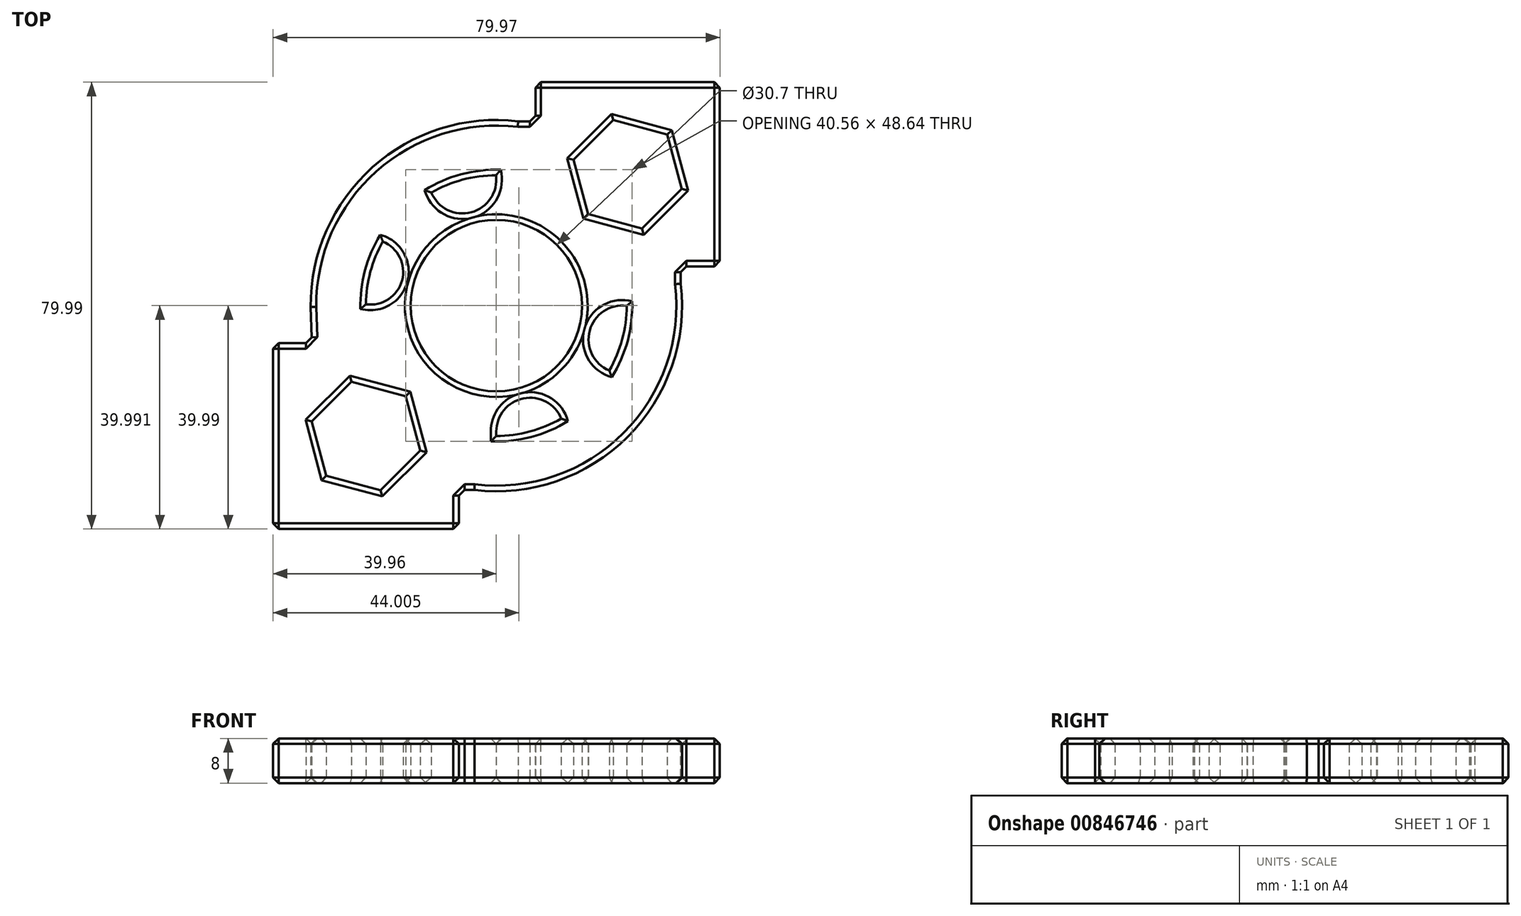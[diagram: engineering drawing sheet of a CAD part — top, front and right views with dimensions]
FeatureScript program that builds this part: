
annotation { "Feature Type Name" : "Feature", "Feature Type Description" : "" }
export const myFeature = defineFeature(function(context is Context, id is Id, definition is map)
    precondition{}
    {
        {
            var Q0;
            Q0=qCreatedBy(makeId("Top.planeOp"),FACE);
            var sketch = newSketch(context, id + "F0", { "sketchPlane" : qUnion([Q0])});
            skCircle(sketch, "E0", {"center": v(0, 0) * mm, "radius": 15.35 * mm});
            skLineSegment(sketch, "E1", {"start": v(0, -33) * mm, "end": v(0, -20.33) * mm});
            skLineSegment(sketch, "E2", {"start": v(0, 16.5) * mm, "end": v(0, 16.5) * mm});
            skLineSegment(sketch, "E3.0", {"start": v(0, 23.33) * mm, "end": v(0, 33) * mm});
            skLineSegment(sketch, "E3.2", {"start": v(26.17, 16.5) * mm, "end": v(26.17, 16.5) * mm});
            skLineSegment(sketch, "E4.0", {"start": v(16.5, 26.16) * mm, "end": v(16.5, 26.17) * mm});
            skLineSegment(sketch, "E4.2", {"start": v(30.17, 16.5) * mm, "end": v(30.17, 16.5) * mm});
            skArc(sketch, "E5.cCircle", {"start": v(20.23, -11.62) * mm, "mid": v(22.57, -5.94) * mm, "end": v(23.33, 0.16) * mm, "construction": true});
            skLineSegment(sketch, "E5.0", {"start": v(16.5, 16.5) * mm, "end": v(16.5, 16.5) * mm});
            skLineSegment(sketch, "E5.1", {"start": v(6.83, -16.5) * mm, "end": v(6.04, -16.5) * mm});
            skCircle(sketch, "E6.cCircle", {"center": v(-16.5, -16.5) * mm, "radius": 23.33 * mm, "construction": true});
            skLineSegment(sketch, "E6.0", {"start": v(0, -20.33) * mm, "end": v(0, -33) * mm});
            skLineSegment(sketch, "E6.1", {"start": v(-3.93, -33) * mm, "end": v(-6.69, -33) * mm});
            skCircle(sketch, "E7.cCircle", {"center": v(-33.17, -33.43) * mm, "radius": 23.76 * mm, "construction": true});
            skLineSegment(sketch, "E7.0", {"start": v(-16.32, -39.83) * mm, "end": v(-16.32, -39.97) * mm});
            skCircle(sketch, "E8.cCircle", {"center": v(-23.32, -23.35) * mm, "radius": 10.05 * mm, "construction": true});
            skLineSegment(sketch, "E8.0", {"start": v(-16.21, -16.24) * mm, "end": v(-13.61, -25.95) * mm});
            skLineSegment(sketch, "E8.1", {"start": v(-13.61, -25.95) * mm, "end": v(-20.72, -33.06) * mm});
            skLineSegment(sketch, "E8.2", {"start": v(-20.72, -33.06) * mm, "end": v(-30.43, -30.46) * mm});
            skLineSegment(sketch, "E8.3", {"start": v(-30.43, -30.46) * mm, "end": v(-33.03, -20.75) * mm});
            skLineSegment(sketch, "E8.4", {"start": v(-33.03, -20.75) * mm, "end": v(-25.92, -13.64) * mm});
            skLineSegment(sketch, "E8.5", {"start": v(-25.92, -13.64) * mm, "end": v(-16.21, -16.24) * mm});
            skLineSegment(sketch, "E9.trimOffspring", {"start": v(-33, -6.73) * mm, "end": v(-33.23, -0.24) * mm});
            skArc(sketch, "E10.cCircle", {"start": v(-23.33, 0.17) * mm, "mid": v(-27.39, -46.5) * mm, "end": v(-15.3, -1.24) * mm, "construction": true});
            skLineSegment(sketch, "E10.0", {"start": v(-6.69, -33) * mm, "end": v(-6.68, -39.97) * mm});
            skLineSegment(sketch, "E10.1", {"start": v(-6.68, -39.97) * mm, "end": v(-39.94, -39.99) * mm});
            skLineSegment(sketch, "E10.2", {"start": v(-39.94, -39.99) * mm, "end": v(-39.96, -6.73) * mm});
            skLineSegment(sketch, "E10.3", {"start": v(-39.96, -6.73) * mm, "end": v(-33, -6.73) * mm});
            skLineSegment(sketch, "E11.trimOffspring", {"start": v(-39.95, -16.68) * mm, "end": v(-39.83, -16.68) * mm});
            skLineSegment(sketch, "E12.trimOffspring", {"start": v(-16.22, -16.24) * mm, "end": v(-16.22, -16.24) * mm});
            skPoint(sketch, "E13.orphan", {"position": v(-6.7, -6.71) * mm});
            skLineSegment(sketch, "E14.trimOffspring", {"start": v(16.23, 16.23) * mm, "end": v(16.4, 16.4) * mm});
            skPoint(sketch, "E15.orphan", {"position": v(30.17, 30.17) * mm});
            skLineSegment(sketch, "E16.0", {"start": v(0, 33) * mm, "end": v(0, 33.23) * mm});
            skLineSegment(sketch, "E16.1", {"start": v(3.9, 33) * mm, "end": v(7, 33) * mm});
            skLineSegment(sketch, "E16.3", {"start": v(33.23, 0) * mm, "end": v(33, 0) * mm});
            skPoint(sketch, "E17.orphan", {"position": v(9.66, 9.67) * mm});
            skLineSegment(sketch, "E18.trimOffspring", {"start": v(33, 7) * mm, "end": v(33, 3.9) * mm});
            skPoint(sketch, "E19.orphan", {"position": v(33, 16.5) * mm});
            skLineSegment(sketch, "E20.trimOffspring", {"start": v(16.5, 26.17) * mm, "end": v(16.5, 26.16) * mm});
            skPoint(sketch, "E21.orphan", {"position": v(33, 33) * mm});
            skLineSegment(sketch, "E22.trimOffspring", {"start": v(16.5, 0) * mm, "end": v(16.5, 0) * mm});
            skArc(sketch, "E23", {"start": v(-20.32, 11.47) * mm, "mid": v(-22.55, 6) * mm, "end": v(-23.33, 0.17) * mm});
            skArc(sketch, "E24", {"start": v(3.9, 33) * mm, "mid": v(-22.16, 24.76) * mm, "end": v(-33.23, -0.24) * mm});
            skArc(sketch, "E25", {"start": v(-11.62, 20.23) * mm, "mid": v(-4.48, 16.7) * mm, "end": v(-0.05, 23.33) * mm});
            skArc(sketch, "E26", {"start": v(-23.33, 0.23) * mm, "mid": v(-16.87, 4.52) * mm, "end": v(-20.32, 11.47) * mm});
            skArc(sketch, "E27", {"start": v(23.33, -0.06) * mm, "mid": v(16.7, -4.48) * mm, "end": v(20.23, -11.62) * mm});
            skArc(sketch, "E28", {"start": v(11.62, -20.23) * mm, "mid": v(4.14, -16.8) * mm, "end": v(0.18, -24.02) * mm});
            skPoint(sketch, "E29.orphan", {"position": v(16.5, -16.5) * mm});
            skPoint(sketch, "E30.orphan", {"position": v(-16.5, 16.5) * mm});
            skLineSegment(sketch, "E31.trimOffspring", {"start": v(0, 22.65) * mm, "end": v(0, 22.43) * mm});
            skPoint(sketch, "E32.start.orphan", {"position": v(0, 33) * mm});
            skCircle(sketch, "E33.cCircle", {"center": v(23.5, 23.5) * mm, "radius": 23.33 * mm, "construction": true});
            skLineSegment(sketch, "E33.1", {"start": v(7, 40) * mm, "end": v(40, 40) * mm});
            skLineSegment(sketch, "E33.2", {"start": v(40, 40) * mm, "end": v(40, 7) * mm});
            skLineSegment(sketch, "E33.3", {"start": v(40, 7) * mm, "end": v(33, 7) * mm});
            skArc(sketch, "E34.trimOffspring", {"start": v(0.17, 23.33) * mm, "mid": v(-5.93, 22.57) * mm, "end": v(-11.62, 20.23) * mm, "construction": true});
            skLineSegment(sketch, "E35.0", {"start": v(16.4, 16.4) * mm, "end": v(13.8, 26.1) * mm});
            skLineSegment(sketch, "E35.1", {"start": v(13.8, 26.1) * mm, "end": v(20.9, 33.2) * mm});
            skLineSegment(sketch, "E35.2", {"start": v(20.9, 33.2) * mm, "end": v(30.61, 30.6) * mm});
            skLineSegment(sketch, "E35.3", {"start": v(30.61, 30.6) * mm, "end": v(33.2, 20.9) * mm});
            skLineSegment(sketch, "E35.4", {"start": v(33.2, 20.9) * mm, "end": v(26.1, 13.79) * mm});
            skLineSegment(sketch, "E35.5", {"start": v(26.1, 13.79) * mm, "end": v(16.4, 16.4) * mm});
            skLineSegment(sketch, "E36.trimOffspring", {"start": v(7, 33) * mm, "end": v(7, 40) * mm});
            skArc(sketch, "E37.trimOffspring", {"start": v(-3.93, -33) * mm, "mid": v(23.5, -23.5) * mm, "end": v(33, 3.9) * mm});
            skArc(sketch, "E38.trimOffspring", {"start": v(-33.17, -2) * mm, "mid": v(-33.17, -2.09) * mm, "end": v(-33.16, -2.17) * mm});
            skArc(sketch, "E39.trimOffspring", {"start": v(-18.04, -14.8) * mm, "mid": v(-16.49, -16.51) * mm, "end": v(-14.77, -18.06) * mm, "construction": true});
            skArc(sketch, "E40.trimOffspring", {"start": v(-20.32, 11.47) * mm, "mid": v(-22.55, 6) * mm, "end": v(-23.33, 0.17) * mm, "construction": true});
            skArc(sketch, "E41.trimOffspring", {"start": v(0.17, 23.33) * mm, "mid": v(-5.93, 22.57) * mm, "end": v(-11.62, 20.23) * mm});
            skArc(sketch, "E42.trimOffspring", {"start": v(16.68, 16.31) * mm, "mid": v(16.6, 16.4) * mm, "end": v(16.5, 16.5) * mm, "construction": true});
            skLineSegment(sketch, "E43.trimOffspring", {"start": v(16.4, 16.4) * mm, "end": v(16.5, 16.5) * mm});
            skArc(sketch, "E44.trimOffspring", {"start": v(-18.04, -14.8) * mm, "mid": v(-16.49, -16.51) * mm, "end": v(-14.77, -18.06) * mm});
            skArc(sketch, "E45.trimOffspring", {"start": v(0, -23.33) * mm, "mid": v(6.01, -22.55) * mm, "end": v(11.62, -20.23) * mm, "construction": true});
            skArc(sketch, "E46.trimOffspring", {"start": v(20.23, -11.62) * mm, "mid": v(22.57, -5.94) * mm, "end": v(23.33, 0.16) * mm});
            skArc(sketch, "E47.trimOffspring", {"start": v(0, -23.33) * mm, "mid": v(6.01, -22.55) * mm, "end": v(11.62, -20.23) * mm});
            skArc(sketch, "E48.trimOffspring", {"start": v(16.68, 16.31) * mm, "mid": v(16.5, 16.5) * mm, "end": v(16.32, 16.68) * mm});
            skSolve(sketch);
        }
        {
            var Q0;
            {var subQ3=sQuery(id+"F0.wireOp",EDGE,"E8.0");var subQ5=sQuery(id+"F0.wireOp",EDGE,"E8.1");var subQ6=makeQuery(id+"F0.imprint","INTERSECT",VERTEX,{"derivedFrom":[subQ3,subQ5]});Q0=makeQuery(id+"F0.imprint","IMPRINT",FACE,{"disambiguationData":[TD([[makeQuery(id+"F0.imprint","IMPRINT",EDGE,{"disambiguationData":[TD([[subQ6,1.0]])],"derivedFrom":subQ3}),1.0]])]});}
            var Q1;
            {var subQ1=sQuery(id+"F0.wireOp",EDGE,"E6.3");var subQ5=sQuery(id+"F0.wireOp",EDGE,"E24");var subQ6=makeQuery(id+"F0.imprint","INTERSECT",VERTEX,{"derivedFrom":[subQ1,subQ5]});Q1=makeQuery(id+"F0.imprint","IMPRINT",FACE,{"disambiguationData":[TD([[makeQuery(id+"F0.imprint","IMPRINT",EDGE,{"disambiguationData":[TD([[subQ6,-1.0]])],"derivedFrom":subQ1}),-1.0]])]});}
            var Q2;
            {var subQ4=sQuery(id+"F0.wireOp",EDGE,"E24");var subQ5=sQuery(id+"F0.wireOp",EDGE,"E3.0");var subQ6=makeQuery(id+"F0.imprint","INTERSECT",VERTEX,{"derivedFrom":[subQ5,subQ4]});Q2=makeQuery(id+"F0.imprint","IMPRINT",FACE,{"disambiguationData":[TD([[makeQuery(id+"F0.imprint","IMPRINT",EDGE,{"disambiguationData":[TD([[subQ6,1.0]])],"derivedFrom":subQ5}),1.0]])]});}
            var Q3;
            {var subQ1=sQuery(id+"F0.wireOp",EDGE,"8dce8ec6-49c2-4d3c-9e0c-89aa3bbadb77.0");var subQ7=sQuery(id+"F0.wireOp",EDGE,"8dce8ec6-49c2-4d3c-9e0c-89aa3bbadb77.1");var subQ9=makeQuery(id+"F0.imprint","INTERSECT",VERTEX,{"derivedFrom":[subQ1,subQ7]});Q3=makeQuery(id+"F0.imprint","IMPRINT",FACE,{"disambiguationData":[TD([[makeQuery(id+"F0.imprint","IMPRINT",EDGE,{"disambiguationData":[TD([[subQ9,1.0]])],"derivedFrom":subQ1}),1.0]])]});}
            var Q4;
            {var subQ4=sQuery(id+"F0.wireOp",EDGE,"E6.1");Q4=makeQuery(id+"F0.imprint","IMPRINT",FACE,{"disambiguationData":[TD([[makeQuery(id+"F0.imprint","IMPRINT",EDGE,{"derivedFrom":subQ4}),-1.0]])]});}
            var Q5;
            {var subQ7=sQuery(id+"F0.wireOp",EDGE,"8dce8ec6-49c2-4d3c-9e0c-89aa3bbadb77.2");Q5=makeQuery(id+"F0.imprint","IMPRINT",FACE,{"disambiguationData":[TD([[makeQuery(id+"F0.imprint","IMPRINT",EDGE,{"derivedFrom":subQ7}),1.0]])]});}
            var Q6;
            {var subQ4=sQuery(id+"F0.wireOp",EDGE,"E16.3");var subQ6=sQuery(id+"F0.wireOp",EDGE,"E24");var subQ8=makeQuery(id+"F0.imprint","INTERSECT",VERTEX,{"derivedFrom":[subQ4,subQ6]});Q6=makeQuery(id+"F0.imprint","IMPRINT",FACE,{"disambiguationData":[TD([[makeQuery(id+"F0.imprint","IMPRINT",EDGE,{"disambiguationData":[TD([[subQ8,-1.0]])],"derivedFrom":subQ4}),1.0]])]});}
            var Q7;
            {var subQ5=sQuery(id+"F0.wireOp",EDGE,"E24");var subQ7=sQuery(id+"F0.wireOp",EDGE,"E3.3");var subQ9=makeQuery(id+"F0.imprint","INTERSECT",VERTEX,{"derivedFrom":[subQ7,subQ5]});Q7=makeQuery(id+"F0.imprint","IMPRINT",FACE,{"disambiguationData":[TD([[makeQuery(id+"F0.imprint","IMPRINT",EDGE,{"disambiguationData":[TD([[subQ9,-1.0]])],"derivedFrom":subQ7}),-1.0]])]});}
            var Q8;
            Q8=makeQuery(id+"F0.imprint","IMPRINT",FACE,{"disambiguationData":[TD([[makeQuery(id+"F0.imprint","IMPRINT",EDGE,{"derivedFrom":sQuery(id+"F0.wireOp",EDGE,"E0")}),-1.0]])]});
            var Q9;
            {var subQ0=sQuery(id+"F0.wireOp",EDGE,"E25");var subQ1=sQuery(id+"F0.wireOp",EDGE,"E23");var subQ2=makeQuery(id+"F0.imprint","INTERSECT",VERTEX,{"disambiguationData":[OD(0.0)],"derivedFrom":[subQ1,subQ0]});Q9=makeQuery(id+"F0.imprint","IMPRINT",FACE,{"disambiguationData":[TD([[makeQuery(id+"F0.imprint","IMPRINT",EDGE,{"disambiguationData":[TD([[subQ2,-1.0]])],"derivedFrom":subQ1}),-1.0]])]});}
            var Q10;
            {var subQ0=sQuery(id+"F0.wireOp",EDGE,"8dce8ec6-49c2-4d3c-9e0c-89aa3bbadb77.5");var subQ1=sQuery(id+"F0.wireOp",EDGE,"8dce8ec6-49c2-4d3c-9e0c-89aa3bbadb77.4");var subQ2=makeQuery(id+"F0.imprint","INTERSECT",VERTEX,{"derivedFrom":[subQ1,subQ0]});Q10=makeQuery(id+"F0.imprint","IMPRINT",FACE,{"disambiguationData":[TD([[makeQuery(id+"F0.imprint","IMPRINT",EDGE,{"disambiguationData":[TD([[subQ2,1.0]])],"derivedFrom":subQ1}),1.0]])]});}
            extrude(context, id + "F1", {"entities" : qUnion([Q0, Q1, Q2, Q3, Q4, Q5, Q6, Q7, Q8, Q9, Q10]), "depth" : 8 * mm, "offsetDistance" : 25 * mm});
        }
        {
            var Q0;
            Q0=makeQuery(id+"F1.opExtrude","CAP_FACE",FACE,{"disambiguationData":[OSD([sQuery(id+"F0.wireOp",EDGE,"E0"),sQuery(id+"F0.wireOp",EDGE,"E6.0"),sQuery(id+"F0.wireOp",EDGE,"E6.1"),sQuery(id+"F0.wireOp",EDGE,"E8.0"),sQuery(id+"F0.wireOp",EDGE,"E8.1"),sQuery(id+"F0.wireOp",EDGE,"E8.2"),sQuery(id+"F0.wireOp",EDGE,"E8.3"),sQuery(id+"F0.wireOp",EDGE,"E8.4"),sQuery(id+"F0.wireOp",EDGE,"E8.5"),sQuery(id+"F0.wireOp",EDGE,"E9.trimOffspring"),sQuery(id+"F0.wireOp",EDGE,"E10.0"),sQuery(id+"F0.wireOp",EDGE,"E10.1"),sQuery(id+"F0.wireOp",EDGE,"E10.2"),sQuery(id+"F0.wireOp",EDGE,"E10.3"),sQuery(id+"F0.wireOp",EDGE,"E16.1"),sQuery(id+"F0.wireOp",EDGE,"E18.trimOffspring"),sQuery(id+"F0.wireOp",EDGE,"E23"),sQuery(id+"F0.wireOp",EDGE,"E24"),sQuery(id+"F0.wireOp",EDGE,"E25"),sQuery(id+"F0.wireOp",EDGE,"E26"),sQuery(id+"F0.wireOp",EDGE,"E27"),sQuery(id+"F0.wireOp",EDGE,"E28"),sQuery(id+"F0.wireOp",EDGE,"E33.1"),sQuery(id+"F0.wireOp",EDGE,"E33.2"),sQuery(id+"F0.wireOp",EDGE,"E33.3"),sQuery(id+"F0.wireOp",EDGE,"E35.0"),sQuery(id+"F0.wireOp",EDGE,"E35.1"),sQuery(id+"F0.wireOp",EDGE,"E35.2"),sQuery(id+"F0.wireOp",EDGE,"E35.3"),sQuery(id+"F0.wireOp",EDGE,"E35.4"),sQuery(id+"F0.wireOp",EDGE,"E35.5"),sQuery(id+"F0.wireOp",EDGE,"E36.trimOffspring"),sQuery(id+"F0.wireOp",EDGE,"E37.trimOffspring"),sQuery(id+"F0.wireOp",EDGE,"E41.trimOffspring"),sQuery(id+"F0.wireOp",EDGE,"E46.trimOffspring"),sQuery(id+"F0.wireOp",EDGE,"E47.trimOffspring")])],"isStart":false});
            var Q1;
            Q1=makeQuery(id+"F1.opExtrude","CAP_FACE",FACE,{"disambiguationData":[OSD([sQuery(id+"F0.wireOp",EDGE,"E0"),sQuery(id+"F0.wireOp",EDGE,"E6.0"),sQuery(id+"F0.wireOp",EDGE,"E6.1"),sQuery(id+"F0.wireOp",EDGE,"E8.0"),sQuery(id+"F0.wireOp",EDGE,"E8.1"),sQuery(id+"F0.wireOp",EDGE,"E8.2"),sQuery(id+"F0.wireOp",EDGE,"E8.3"),sQuery(id+"F0.wireOp",EDGE,"E8.4"),sQuery(id+"F0.wireOp",EDGE,"E8.5"),sQuery(id+"F0.wireOp",EDGE,"E9.trimOffspring"),sQuery(id+"F0.wireOp",EDGE,"E10.0"),sQuery(id+"F0.wireOp",EDGE,"E10.1"),sQuery(id+"F0.wireOp",EDGE,"E10.2"),sQuery(id+"F0.wireOp",EDGE,"E10.3"),sQuery(id+"F0.wireOp",EDGE,"E16.1"),sQuery(id+"F0.wireOp",EDGE,"E18.trimOffspring"),sQuery(id+"F0.wireOp",EDGE,"E23"),sQuery(id+"F0.wireOp",EDGE,"E24"),sQuery(id+"F0.wireOp",EDGE,"E25"),sQuery(id+"F0.wireOp",EDGE,"E26"),sQuery(id+"F0.wireOp",EDGE,"E27"),sQuery(id+"F0.wireOp",EDGE,"E28"),sQuery(id+"F0.wireOp",EDGE,"E33.1"),sQuery(id+"F0.wireOp",EDGE,"E33.2"),sQuery(id+"F0.wireOp",EDGE,"E33.3"),sQuery(id+"F0.wireOp",EDGE,"E35.0"),sQuery(id+"F0.wireOp",EDGE,"E35.1"),sQuery(id+"F0.wireOp",EDGE,"E35.2"),sQuery(id+"F0.wireOp",EDGE,"E35.3"),sQuery(id+"F0.wireOp",EDGE,"E35.4"),sQuery(id+"F0.wireOp",EDGE,"E35.5"),sQuery(id+"F0.wireOp",EDGE,"E36.trimOffspring"),sQuery(id+"F0.wireOp",EDGE,"E37.trimOffspring"),sQuery(id+"F0.wireOp",EDGE,"E41.trimOffspring"),sQuery(id+"F0.wireOp",EDGE,"E46.trimOffspring"),sQuery(id+"F0.wireOp",EDGE,"E47.trimOffspring")])],"isStart":true});
            var Q2;
            Q2=makeQuery(id+"F1.opExtrude","SWEPT_EDGE",EDGE,{"disambiguationData":[OSD([sQuery(id+"F0.wireOp",EDGE,"E10.1"),sQuery(id+"F0.wireOp",EDGE,"E10.2")])]});
            var Q3;
            Q3=makeQuery(id+"F1.opExtrude","SWEPT_EDGE",EDGE,{"disambiguationData":[OSD([sQuery(id+"F0.wireOp",EDGE,"E10.2"),sQuery(id+"F0.wireOp",EDGE,"E10.3")])]});
            var Q4;
            Q4=makeQuery(id+"F1.opExtrude","SWEPT_EDGE",EDGE,{"disambiguationData":[OSD([sQuery(id+"F0.wireOp",EDGE,"E9.trimOffspring"),sQuery(id+"F0.wireOp",EDGE,"E10.3")])]});
            var Q5;
            Q5=makeQuery(id+"F1.opExtrude","SWEPT_EDGE",EDGE,{"disambiguationData":[OSD([sQuery(id+"F0.wireOp",EDGE,"E16.1"),sQuery(id+"F0.wireOp",EDGE,"E36.trimOffspring")])]});
            var Q6;
            Q6=makeQuery(id+"F1.opExtrude","SWEPT_EDGE",EDGE,{"disambiguationData":[OSD([sQuery(id+"F0.wireOp",EDGE,"E33.1"),sQuery(id+"F0.wireOp",EDGE,"E36.trimOffspring")])]});
            var Q7;
            Q7=makeQuery(id+"F1.opExtrude","SWEPT_EDGE",EDGE,{"disambiguationData":[OSD([sQuery(id+"F0.wireOp",EDGE,"E33.1"),sQuery(id+"F0.wireOp",EDGE,"E33.2")])]});
            var Q8;
            Q8=makeQuery(id+"F1.opExtrude","SWEPT_EDGE",EDGE,{"disambiguationData":[OSD([sQuery(id+"F0.wireOp",EDGE,"E18.trimOffspring"),sQuery(id+"F0.wireOp",EDGE,"E33.3")])]});
            var Q9;
            Q9=makeQuery(id+"F1.opExtrude","SWEPT_EDGE",EDGE,{"disambiguationData":[OSD([sQuery(id+"F0.wireOp",EDGE,"E33.2"),sQuery(id+"F0.wireOp",EDGE,"E33.3")])]});
            var Q10;
            Q10=makeQuery(id+"F1.opExtrude","SWEPT_EDGE",EDGE,{"disambiguationData":[OSD([sQuery(id+"F0.wireOp",EDGE,"E6.1"),sQuery(id+"F0.wireOp",EDGE,"E10.0")])]});
            var Q11;
            Q11=makeQuery(id+"F1.opExtrude","SWEPT_EDGE",EDGE,{"disambiguationData":[OSD([sQuery(id+"F0.wireOp",EDGE,"E10.0"),sQuery(id+"F0.wireOp",EDGE,"E10.1")])]});
            chamfer(context, id + "F2", {"entities" : qUnion([Q0, Q1, Q2, Q3, Q4, Q5, Q6, Q7, Q8, Q9, Q10, Q11]), "width" : 1 * mm, "tangentPropagation" : true});
        }
    });
